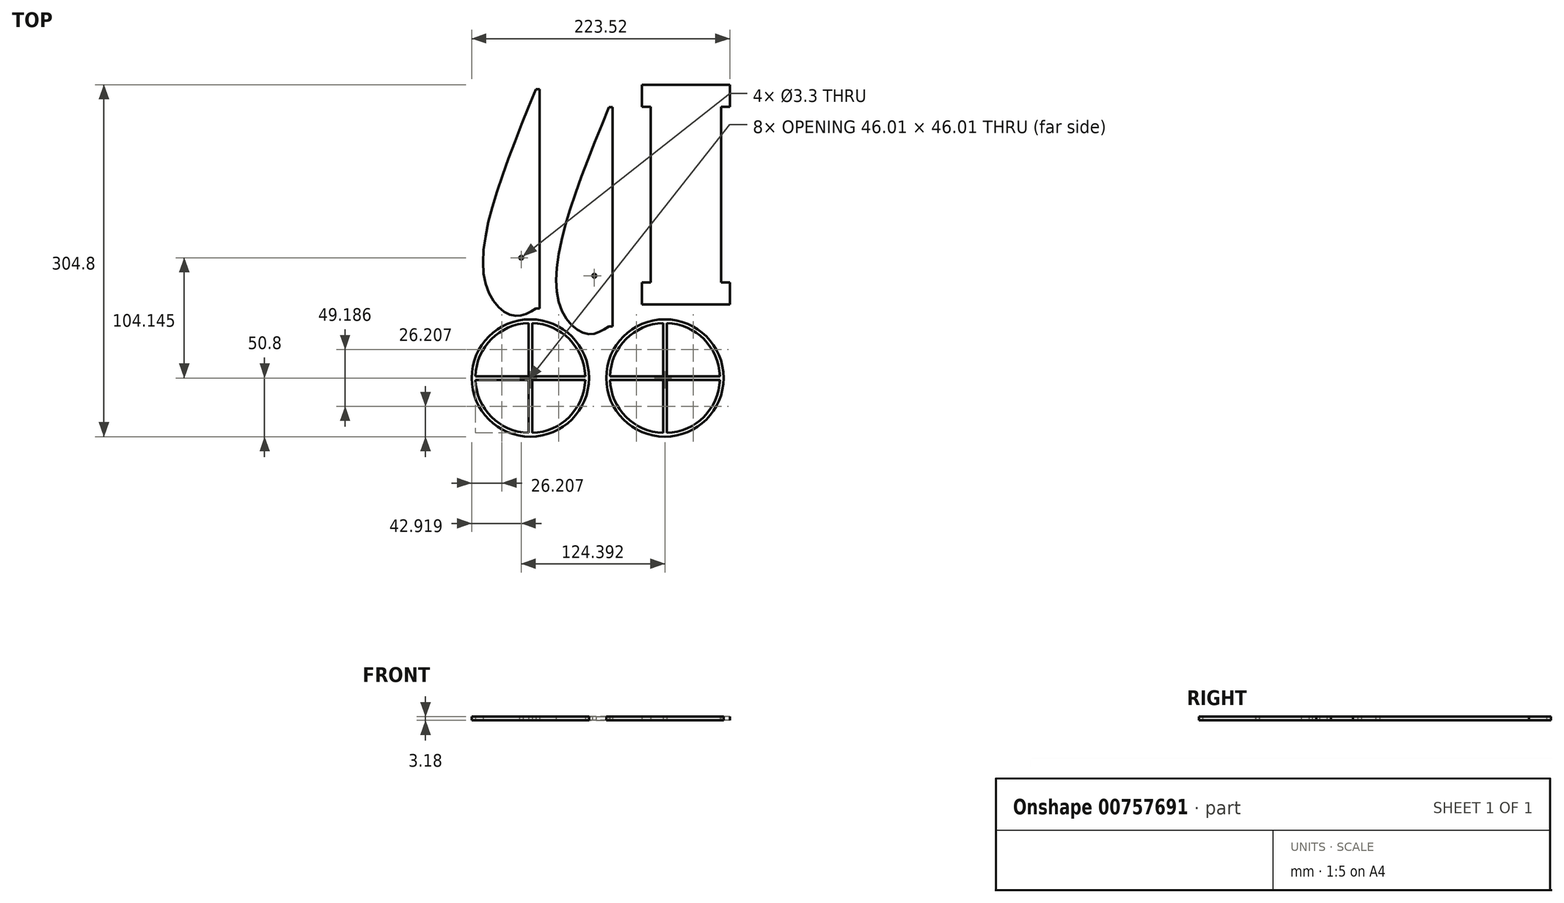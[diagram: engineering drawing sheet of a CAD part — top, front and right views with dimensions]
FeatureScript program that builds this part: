
annotation { "Feature Type Name" : "Feature", "Feature Type Description" : "" }
export const myFeature = defineFeature(function(context is Context, id is Id, definition is map)
    precondition{}
    {
        {
            var Q0;
            Q0=qCreatedBy(makeId("Top.planeOp"),FACE);
            var sketch = newSketch(context, id + "F0", { "sketchPlane" : qUnion([Q0])});
            skLineSegment(sketch, "E0.bottom", {"start": v(152.4, -152.4) * mm, "end": v(-152.4, -152.4) * mm});
            skLineSegment(sketch, "E0.left", {"start": v(152.4, -152.4) * mm, "end": v(152.4, 152.4) * mm});
            skLineSegment(sketch, "E0.right", {"start": v(-152.4, -152.4) * mm, "end": v(-152.4, 152.4) * mm});
            skPoint(sketch, "E0.middle", {"position": v(0, 0) * mm});
            skPoint(sketch, "E1", {"position": v(-101.6, -101.6) * mm});
            skCircle(sketch, "E2", {"center": v(-101.6, -101.6) * mm, "radius": 50.8 * mm});
            skLineSegment(sketch, "E3", {"start": v(-103.19, -100.01) * mm, "end": v(-103.19, -54) * mm});
            skLineSegment(sketch, "E4", {"start": v(-103.19, -103.19) * mm, "end": v(-103.19, -149.2) * mm});
            skLineSegment(sketch, "E5", {"start": v(-100.02, -54) * mm, "end": v(-100.02, -100.01) * mm});
            skArc(sketch, "E6", {"start": v(-103.19, -54) * mm, "mid": v(-135.28, -67.92) * mm, "end": v(-149.2, -100.01) * mm});
            skArc(sketch, "E7.trimOffspring", {"start": v(-100.02, -149.2) * mm, "mid": v(-67.93, -135.28) * mm, "end": v(-54, -103.19) * mm});
            skLineSegment(sketch, "E8", {"start": v(-149.2, -100.01) * mm, "end": v(-103.19, -100.01) * mm});
            skLineSegment(sketch, "E9", {"start": v(-149.2, -103.19) * mm, "end": v(-103.19, -103.19) * mm});
            skLineSegment(sketch, "E10.trimOffspring", {"start": v(-100.02, -100.01) * mm, "end": v(-54, -100.01) * mm});
            skLineSegment(sketch, "E11.trimOffspring", {"start": v(-100.02, -103.19) * mm, "end": v(-54, -103.19) * mm});
            skLineSegment(sketch, "E12.trimOffspring", {"start": v(-100.02, -103.19) * mm, "end": v(-100.02, -149.2) * mm});
            skArc(sketch, "E13.trimOffspring", {"start": v(-149.2, -103.19) * mm, "mid": v(-135.28, -135.28) * mm, "end": v(-103.19, -149.2) * mm});
            skArc(sketch, "E14.trimOffspring", {"start": v(-54, -100.01) * mm, "mid": v(-67.93, -67.92) * mm, "end": v(-100.02, -54) * mm});
            skCircle(sketch, "E15", {"center": v(14.91, -101.6) * mm, "radius": 50.8 * mm});
            skLineSegment(sketch, "E16", {"start": v(13.32, -100.01) * mm, "end": v(13.32, -54) * mm});
            skLineSegment(sketch, "E17", {"start": v(13.32, -103.19) * mm, "end": v(13.32, -149.2) * mm});
            skLineSegment(sketch, "E18", {"start": v(16.5, -54) * mm, "end": v(16.5, -100.01) * mm});
            skArc(sketch, "E19", {"start": v(13.32, -54) * mm, "mid": v(-18.77, -67.92) * mm, "end": v(-32.69, -100.01) * mm});
            skArc(sketch, "E20.trimOffspring", {"start": v(16.5, -149.2) * mm, "mid": v(48.59, -135.28) * mm, "end": v(62.5, -103.19) * mm});
            skLineSegment(sketch, "E21", {"start": v(-32.69, -100.01) * mm, "end": v(13.32, -100.01) * mm});
            skLineSegment(sketch, "E22", {"start": v(-32.69, -103.19) * mm, "end": v(13.32, -103.19) * mm});
            skLineSegment(sketch, "E23.trimOffspring", {"start": v(16.5, -100.01) * mm, "end": v(62.5, -100.01) * mm});
            skLineSegment(sketch, "E24.trimOffspring", {"start": v(16.5, -103.19) * mm, "end": v(62.5, -103.19) * mm});
            skLineSegment(sketch, "E25.trimOffspring", {"start": v(16.5, -103.19) * mm, "end": v(16.5, -149.2) * mm});
            skArc(sketch, "E26.trimOffspring", {"start": v(-32.69, -103.19) * mm, "mid": v(-18.77, -135.28) * mm, "end": v(13.32, -149.2) * mm});
            skArc(sketch, "E27.trimOffspring", {"start": v(62.5, -100.01) * mm, "mid": v(48.59, -67.92) * mm, "end": v(16.5, -54) * mm});
            skLineSegment(sketch, "E28", {"start": v(-152.4, 152.4) * mm, "end": v(-5.08, 152.4) * mm});
            skCircle(sketch, "E29", {"center": v(-101.6, -101.6) * mm, "radius": 1.65 * mm});
            skCircle(sketch, "E30", {"center": v(14.91, -101.6) * mm, "radius": 1.65 * mm});
            skPoint(sketch, "E31", {"position": v(-109.48, 2.54) * mm});
            skCircle(sketch, "E32", {"center": v(-109.48, 2.54) * mm, "radius": 1.65 * mm});
            skLineSegment(sketch, "E33.bottom", {"start": v(71.12, 152.4) * mm, "end": v(-5.08, 152.4) * mm});
            skLineSegment(sketch, "E33.top", {"start": v(71.12, 133.35) * mm, "end": v(63.5, 133.35) * mm});
            skLineSegment(sketch, "E33.left", {"start": v(71.12, 152.4) * mm, "end": v(71.12, 133.35) * mm});
            skLineSegment(sketch, "E33.right", {"start": v(-5.08, 152.4) * mm, "end": v(-5.08, 133.35) * mm});
            skLineSegment(sketch, "E34.trimOffspring", {"start": v(71.12, 152.4) * mm, "end": v(152.4, 152.4) * mm});
            skLineSegment(sketch, "E35.trimOffspring", {"start": v(2.54, 133.35) * mm, "end": v(-5.08, 133.35) * mm});
            skPoint(sketch, "E36.orphan", {"position": v(33.02, 133.35) * mm});
            skLineSegment(sketch, "E37", {"start": v(-5.08, 133.35) * mm, "end": v(2.54, 133.35) * mm});
            skFitSpline(sketch, "E38", {"points": [v(-96.78, 148.6) * mm, v(-141.23, -16.5) * mm, v(-115.83, -47.72) * mm, v(-96.78, -41.37) * mm], "startDerivative": vector(-143.2, -351.2) * mm, "endDerivative": vector(96.6, 60.25) * mm});
            skFitSpline(sketch, "E39", {"points": [v(-33.5, 132.97) * mm, v(-77.94, -32.13) * mm, v(-52.54, -63.34) * mm, v(-33.5, -57) * mm], "startDerivative": vector(-143.2, -351.2) * mm, "endDerivative": vector(96.6, 60.25) * mm});
            skLineSegment(sketch, "E40", {"start": v(2.54, 133.35) * mm, "end": v(2.54, -18.97) * mm});
            skLineSegment(sketch, "E41", {"start": v(63.5, 133.35) * mm, "end": v(63.5, -18.97) * mm});
            skLineSegment(sketch, "E42", {"start": v(2.54, -18.97) * mm, "end": v(-5.08, -18.97) * mm});
            skLineSegment(sketch, "E43", {"start": v(-5.08, -18.97) * mm, "end": v(-5.08, -38.02) * mm});
            skLineSegment(sketch, "E44", {"start": v(-5.08, -38.02) * mm, "end": v(71.12, -38.02) * mm});
            skLineSegment(sketch, "E45", {"start": v(71.12, -38.02) * mm, "end": v(71.12, -18.97) * mm});
            skLineSegment(sketch, "E46", {"start": v(71.12, -18.97) * mm, "end": v(63.5, -18.97) * mm});
            skCircle(sketch, "E47", {"center": v(-46.2, -13.08) * mm, "radius": 1.65 * mm});
            skLineSegment(sketch, "E48", {"start": v(-96.78, 148.6) * mm, "end": v(-93.6, 148.6) * mm});
            skLineSegment(sketch, "E49", {"start": v(-93.6, 148.6) * mm, "end": v(-93.6, -41.37) * mm});
            skLineSegment(sketch, "E50", {"start": v(-96.78, -41.37) * mm, "end": v(-93.6, -41.37) * mm});
            skLineSegment(sketch, "E51.bottom", {"start": v(-33.5, -57) * mm, "end": v(-30.32, -57) * mm});
            skLineSegment(sketch, "E51.top", {"start": v(-33.5, 132.97) * mm, "end": v(-30.32, 132.97) * mm});
            skLineSegment(sketch, "E51.right", {"start": v(-30.32, -57) * mm, "end": v(-30.32, 132.97) * mm});
            skSolve(sketch);
        }
        {
            var Q0;
            Q0=makeQuery(id+"F0.imprint","IMPRINT",FACE,{"disambiguationData":[TD([[makeQuery(id+"F0.imprint","IMPRINT",EDGE,{"derivedFrom":sQuery(id+"F0.wireOp",EDGE,"E15")}),1.0]])]});
            var Q1;
            Q1=makeQuery(id+"F0.imprint","IMPRINT",FACE,{"disambiguationData":[TD([[makeQuery(id+"F0.imprint","IMPRINT",EDGE,{"derivedFrom":sQuery(id+"F0.wireOp",EDGE,"98997905-2f13-42c9-b917-e8bb11a4a756")}),1.0]])]});
            var Q2;
            Q2=makeQuery(id+"F0.imprint","IMPRINT",FACE,{"disambiguationData":[TD([[makeQuery(id+"F0.imprint","IMPRINT",EDGE,{"derivedFrom":sQuery(id+"F0.wireOp",EDGE,"E3")}),-1.0]])]});
            var Q3;
            Q3=makeQuery(id+"F0.imprint","IMPRINT",FACE,{"disambiguationData":[TD([[makeQuery(id+"F0.imprint","IMPRINT",EDGE,{"derivedFrom":sQuery(id+"F0.wireOp",EDGE,"31dc7c77-72cc-4573-9705-13972d63c62a")}),1.0]])]});
            var Q4;
            {var subQ6=sQuery(id+"F0.wireOp",EDGE,"SPsJpwIS-kOOs-LNO5-Mm5u-aHKrSvhFCvLY");Q4=makeQuery(id+"F0.imprint","IMPRINT",FACE,{"disambiguationData":[TD([[makeQuery(id+"F0.imprint","IMPRINT",EDGE,{"derivedFrom":subQ6}),-1.0]])]});}
            var Q5;
            Q5=makeQuery(id+"F0.imprint","IMPRINT",FACE,{"disambiguationData":[TD([[makeQuery(id+"F0.imprint","IMPRINT",EDGE,{"derivedFrom":sQuery(id+"F0.wireOp",EDGE,"E33.bottom")}),1.0]])]});
            var Q6;
            Q6=makeQuery(id+"F0.imprint","IMPRINT",FACE,{"disambiguationData":[TD([[makeQuery(id+"F0.imprint","IMPRINT",EDGE,{"derivedFrom":sQuery(id+"F0.wireOp",EDGE,"E32")}),-1.0]])]});
            var Q7;
            Q7=makeQuery(id+"F0.imprint","IMPRINT",FACE,{"disambiguationData":[TD([[makeQuery(id+"F0.imprint","IMPRINT",EDGE,{"derivedFrom":sQuery(id+"F0.wireOp",EDGE,"6oiHb1xW-9w4z-8BhH-qTWl-JfAxZ4tyxuDM")}),-1.0]])]});
            var Q8;
            Q8=makeQuery(id+"F0.imprint","IMPRINT",FACE,{"disambiguationData":[TD([[makeQuery(id+"F0.imprint","IMPRINT",EDGE,{"derivedFrom":sQuery(id+"F0.wireOp",EDGE,"a535dd24-1488-4dd1-b95b-1157a4d89cdc")}),1.0]])]});
            var Q9;
            Q9=makeQuery(id+"F0.imprint","IMPRINT",FACE,{"disambiguationData":[TD([[makeQuery(id+"F0.imprint","IMPRINT",EDGE,{"derivedFrom":sQuery(id+"F0.wireOp",EDGE,"E47")}),-1.0]])]});
            extrude(context, id + "F1", {"entities" : qUnion([Q0, Q1, Q2, Q3, Q4, Q5, Q6, Q7, Q8, Q9]), "depth" : 3.17 * mm, "offsetDistance" : 25.4 * mm});
        }
    });
